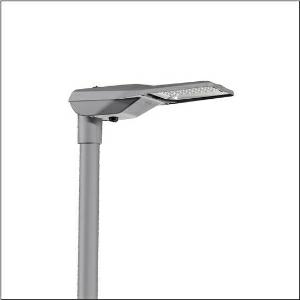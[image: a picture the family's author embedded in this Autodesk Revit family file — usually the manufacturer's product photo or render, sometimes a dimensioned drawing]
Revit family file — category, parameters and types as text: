
# Revit family: streetlight_sl_21_iq_mini___st1_0a_5xe2d61y08gb_62ef
name_source: partatom
category: Lighting Fixtures
units: mm (PartAtom-declared; Revit-internal decimal feet)

## family parameters
Cut with Voids When Loaded = No
Host = Face
Light Source = No
Part Type = Normal
Room Calculation Point = No
Round Connector Dimension = Use Diameter
Shared = No

## types (1)
- --- (1 x LED, 5200 lm, 39.8 W, 2700K)
    Apparent Load = 40 VA
    CIE Flux Codes = 37 72 97 100 100
    Color Rendering = 70
    Color Temperature = 2700K
    Default Elevation = 1800 mm
    Description = Streetlight SL 21 iQ mini, mast luminaire, primary light control with lens, of PMMA, primary optical cover: cover, of toughened safety glass, transparent, light distribution: ST1.0a, light emission: direct distribution, primary light characteristic: asymmetric, installation type: post-top, side-entry, LED, High Power LED, rated luminous flux: 5.200lm, luminous efficacy: 131lm/W, light colour: 727, colour temperature: 2700K, control gear: iQ-Street Remote, D4i with power reduction, control: pre-setting: logarithmic dimming characteristic, Street-Remote, Auto-Match, Temp-Guard, Lumen-Switch, Night-Set, Smart-Wire, Light-Fading, Desk-Remote (wireless, voltage-free reading and setting of iQ features in the workshop via application-optimized NFC function/RFID function), optimised constant luminous flux control (CLO 2.0), mains connection: 220..240V, AC, 50/60Hz, start of lifetime: 40W, end of service life: 41W, reduction: 18W, luminaire housing, of diecast aluminium, powder-coated, Siteco® metallic grey (DB 702S), corrosivity category C5 mid according to DIN EN ISO 12944, please order mast flange separately, inclination adjustable: 0°, 5°, 10°, 15°, sealing non-destructively replaceable, multi-level sealing system, length: 628mm, width: 235mm, height: 110mm, mast flange for spigot size: 42mm (side-entry): 5XC10008XM4, 60/48mm (side-entry/post-top): 5XC10108XM2, 76/60mm (side-entry/post-top): 5XC10108XM1, mounting height: 4..8m, Smart Interface below and above, protection rating (complete): IP66, insulation class (complete): insulation class II (safety insulation), certification: CE, ENEC, ENEC+, VDE, impact resistance: IK10, permissible operating ambient temperature for outdoor applications: -40..+50°C, standard-compliant lighting for roads and squares, packaging unit: 1 piece

Light Distribution: ST1.0a
    Height = 110 mm
    Lamp = 1 x LED
    Lamp Light Flux = 5200 lm
    Lamp Power = 39.8 W
    Lamp count = 1
    Length = 625 mm
    Luminous efficacy = 131 lm/W
    Manufacturer = Siteco
    ModVariant = No
    Model = 5XE2D61Y08GB
    Number of Poles = 1
    OnlyDefault = Yes
    Power Factor = 1
    Product Name = Streetlight SL 21 iQ mini | ST1.0a
    Product group = mast luminaire | pylon top
    ProductGroupID = 6100
    Protection Class = Protection class II
    Protection Degree = IP 66
    RLX_Detail_Level = 1
    RLX_Emergency_Light_Flux = 0 lm
    RLX_Emergency_Type = 0
    RLX_Emergency_Type_DB = No
    RlxData = <blob elided: 26829 chars, md5=d6082dd9>
    Socket = socket
    Standby Power = 0 W
    System Light Flux = 5200 lm
    System Power = 40 W
    Type Comments = factory setting: luminous flux: 100 % | dim-lin: 254 | 800 mA
    Type Image = l_1003514.jpg
    URL = http://relux.com
    VarID = @adj_114992
    Voltage = 0 V
    Weight = 0.00 kg
    Width = 234 mm

## geometry (parser evidence)
native form markers: Blend x4, Sweep x9
no freeform markers — native parametric forms only
